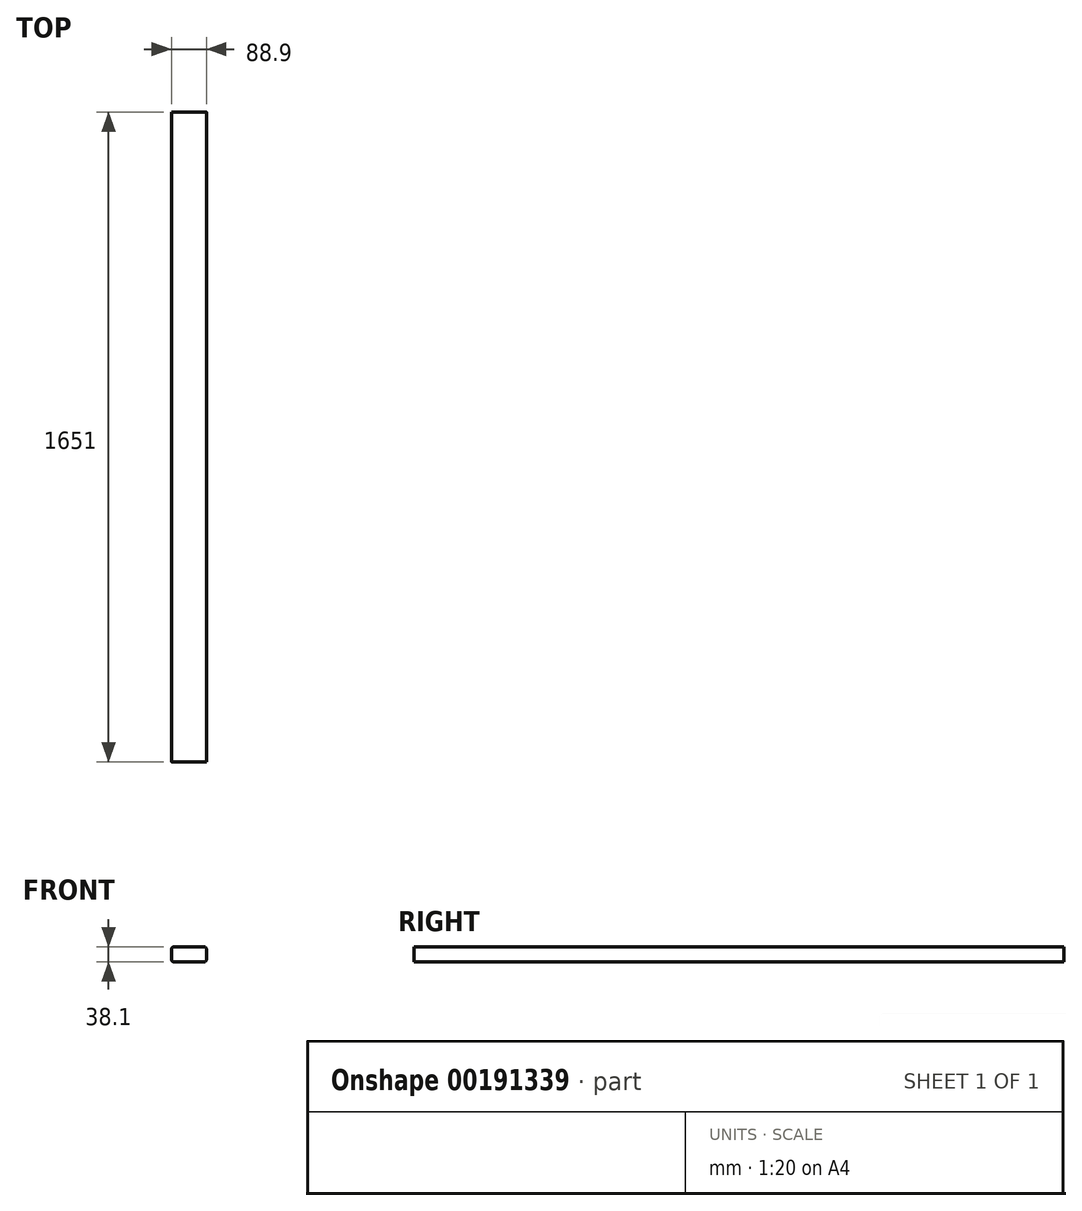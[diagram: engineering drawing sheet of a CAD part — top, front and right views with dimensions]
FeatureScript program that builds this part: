
annotation { "Feature Type Name" : "Feature", "Feature Type Description" : "" }
export const myFeature = defineFeature(function(context is Context, id is Id, definition is map)
    precondition{}
    {
        {
            var Q0;
            Q0=qCreatedBy(makeId("Front.planeOp"),FACE);
            var sketch = newSketch(context, id + "F0", { "sketchPlane" : qUnion([Q0])});
            skLineSegment(sketch, "E0.bottom", {"start": v(-38.1, 19.05) * mm, "end": v(38.1, 19.05) * mm});
            skLineSegment(sketch, "E0.top", {"start": v(-38.1, -19.05) * mm, "end": v(38.1, -19.05) * mm});
            skLineSegment(sketch, "E0.left", {"start": v(-44.45, 12.7) * mm, "end": v(-44.45, -12.7) * mm});
            skLineSegment(sketch, "E0.right", {"start": v(44.45, 12.7) * mm, "end": v(44.45, -12.7) * mm});
            skPoint(sketch, "E0.middle", {"position": v(0, 0) * mm});
            skPoint(sketch, "E1.visualSharp", {"position": v(-44.45, 19.05) * mm});
            skArc(sketch, "E1.filletArc", {"start": v(-38.1, 19.05) * mm, "mid": v(-42.6, 17.2) * mm, "end": v(-44.45, 12.7) * mm});
            skPoint(sketch, "E2.visualSharp", {"position": v(-44.45, -19.05) * mm});
            skArc(sketch, "E2.filletArc", {"start": v(-44.45, -12.7) * mm, "mid": v(-42.6, -17.2) * mm, "end": v(-38.1, -19.05) * mm});
            skPoint(sketch, "E3.visualSharp", {"position": v(44.45, -19.05) * mm});
            skArc(sketch, "E3.filletArc", {"start": v(38.1, -19.05) * mm, "mid": v(42.6, -17.2) * mm, "end": v(44.45, -12.7) * mm});
            skPoint(sketch, "E4.visualSharp", {"position": v(44.45, 19.05) * mm});
            skArc(sketch, "E4.filletArc", {"start": v(44.45, 12.7) * mm, "mid": v(42.6, 17.2) * mm, "end": v(38.1, 19.05) * mm});
            skSolve(sketch);
        }
        {
            var Q0;
            Q0=makeQuery(id+"F0.imprint","IMPRINT",FACE,{"disambiguationData":[TD([[makeQuery(id+"F0.imprint","IMPRINT",EDGE,{"derivedFrom":sQuery(id+"F0.wireOp",EDGE,"E0.bottom")}),-1.0]])]});
            extrude(context, id + "F1", {"entities" : qUnion([Q0]), "depth" : 1651 * mm});
        }
    });
